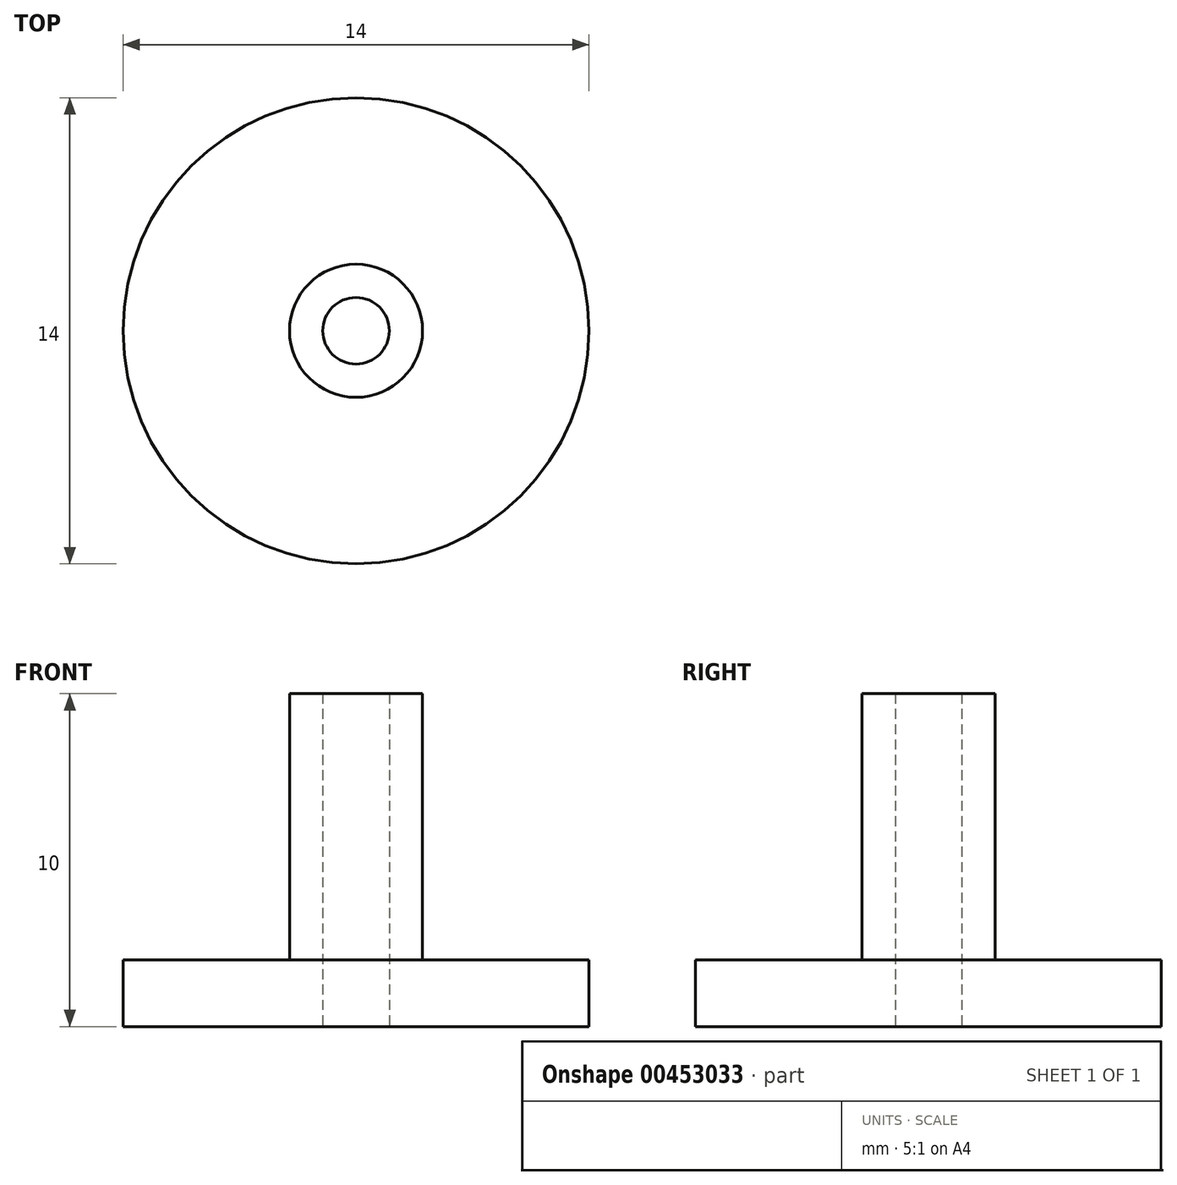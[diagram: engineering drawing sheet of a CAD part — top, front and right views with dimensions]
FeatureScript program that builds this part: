
annotation { "Feature Type Name" : "Feature", "Feature Type Description" : "" }
export const myFeature = defineFeature(function(context is Context, id is Id, definition is map)
    precondition{}
    {
        {
            var Q0;
            Q0=qCreatedBy(makeId("Top.planeOp"),FACE);
            var sketch = newSketch(context, id + "F0", { "sketchPlane" : qUnion([Q0])});
            skCircle(sketch, "E0", {"center": v(0, 0) * mm, "radius": 7 * mm});
            skCircle(sketch, "E1", {"center": v(0, 0) * mm, "radius": 1 * mm});
            skCircle(sketch, "E2", {"center": v(0, 0) * mm, "radius": 2 * mm});
            skLineSegment(sketch, "E3", {"start": v(0, 7) * mm, "end": v(0, -7) * mm});
            skSolve(sketch);
        }
        {
            var Q0;
            {var subQ0=sQuery(id+"F0.wireOp",EDGE,"E3");var subQ1=sQuery(id+"F0.wireOp",EDGE,"E0");var subQ2=makeQuery(id+"F0.imprint","INTERSECT",VERTEX,{"disambiguationData":[OD(0.0)],"derivedFrom":[subQ1,subQ0]});Q0=makeQuery(id+"F0.imprint","IMPRINT",FACE,{"disambiguationData":[TD([[makeQuery(id+"F0.imprint","IMPRINT",EDGE,{"disambiguationData":[TD([[subQ2,1.0]])],"derivedFrom":subQ1}),1.0]])]});}
            extrude(context, id + "F1", {"entities" : qUnion([Q0]), "depth" : 2 * mm});
        }
        {
            var Q0;
            {var subQ0=sQuery(id+"F0.wireOp",EDGE,"E3");var subQ1=sQuery(id+"F0.wireOp",EDGE,"E0");var subQ2=makeQuery(id+"F0.imprint","INTERSECT",VERTEX,{"disambiguationData":[OD(0.0)],"derivedFrom":[subQ1,subQ0]});Q0=makeQuery(id+"F0.imprint","IMPRINT",FACE,{"disambiguationData":[TD([[makeQuery(id+"F0.imprint","IMPRINT",EDGE,{"disambiguationData":[TD([[subQ2,-1.0]])],"derivedFrom":subQ1}),1.0]])]});}
            extrude(context, id + "F2", {"entities" : qUnion([Q0]), "depth" : 2 * mm});
        }
        {
            var Q0;
            {var subQ0=sQuery(id+"F0.wireOp",EDGE,"E3");var subQ1=sQuery(id+"F0.wireOp",EDGE,"E1");var subQ2=makeQuery(id+"F0.imprint","INTERSECT",VERTEX,{"disambiguationData":[OD(0.0)],"derivedFrom":[subQ1,subQ0]});Q0=makeQuery(id+"F0.imprint","IMPRINT",FACE,{"disambiguationData":[TD([[makeQuery(id+"F0.imprint","IMPRINT",EDGE,{"disambiguationData":[TD([[subQ2,-1.0]])],"derivedFrom":subQ1}),-1.0]])]});}
            var Q1;
            {var subQ0=sQuery(id+"F0.wireOp",EDGE,"E3");var subQ1=sQuery(id+"F0.wireOp",EDGE,"E1");var subQ2=makeQuery(id+"F0.imprint","INTERSECT",VERTEX,{"disambiguationData":[OD(0.0)],"derivedFrom":[subQ1,subQ0]});Q1=makeQuery(id+"F0.imprint","IMPRINT",FACE,{"disambiguationData":[TD([[makeQuery(id+"F0.imprint","IMPRINT",EDGE,{"disambiguationData":[TD([[subQ2,1.0]])],"derivedFrom":subQ1}),-1.0]])]});}
            extrude(context, id + "F3", {"entities" : qUnion([Q0, Q1]), "operationType" : NewBodyOperationType.ADD, "depth" : 10 * mm});
        }
    });
